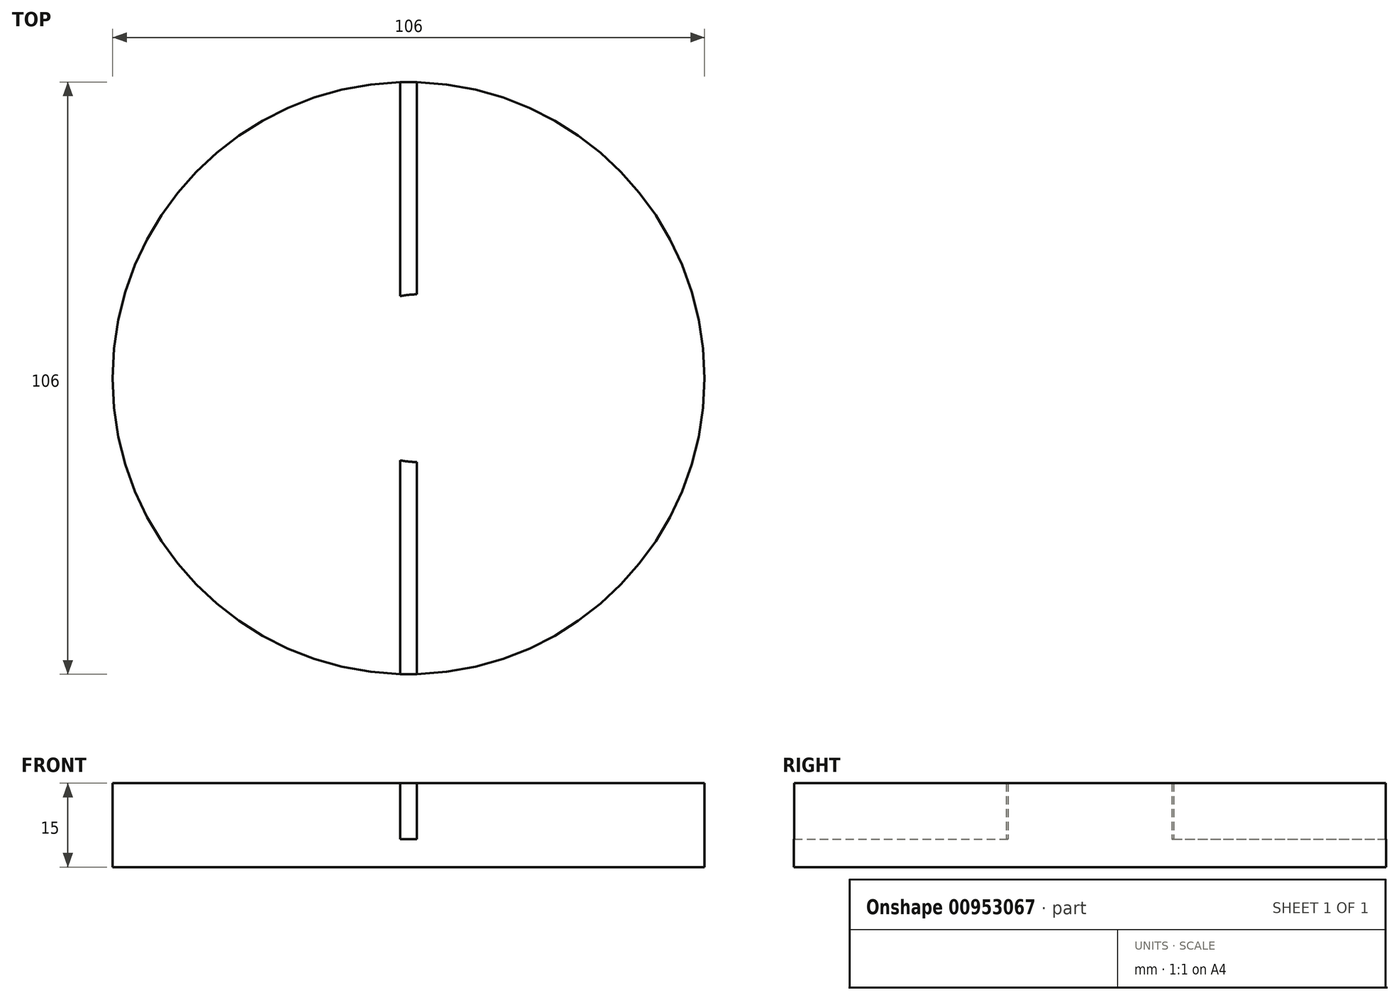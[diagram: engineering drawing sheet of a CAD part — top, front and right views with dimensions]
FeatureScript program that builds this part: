
annotation { "Feature Type Name" : "Feature", "Feature Type Description" : "" }
export const myFeature = defineFeature(function(context is Context, id is Id, definition is map)
    precondition{}
    {
        {
            var Q0;
            Q0=qCreatedBy(makeId("Top.planeOp"),FACE);
            var sketch = newSketch(context, id + "F0", { "sketchPlane" : qUnion([Q0])});
            skCircle(sketch, "E0", {"center": v(0, 0) * mm, "radius": 53 * mm});
            skSolve(sketch);
        }
        {
            var Q0;
            Q0=makeQuery(id+"F0.imprint","IMPRINT",FACE,{"disambiguationData":[TD([[makeQuery(id+"F0.imprint","IMPRINT",EDGE,{"derivedFrom":sQuery(id+"F0.wireOp",EDGE,"E0")}),1.0]])]});
            extrude(context, id + "F1", {"entities" : qUnion([Q0]), "depth" : 15 * mm, "offsetDistance" : 25 * mm});
        }
        {
            var Q0;
            Q0=makeQuery(id+"F1.opExtrude","CAP_FACE",FACE,{"disambiguationData":[OSD([sQuery(id+"F0.wireOp",EDGE,"E0")])],"isStart":false});
            var sketch = newSketch(context, id + "F2", { "sketchPlane" : qUnion([Q0])});
            skLineSegment(sketch, "E1.bottom", {"start": v(1.5, -75) * mm, "end": v(-1.5, -75) * mm});
            skLineSegment(sketch, "E1.top", {"start": v(1.5, 75) * mm, "end": v(-1.5, 75) * mm});
            skLineSegment(sketch, "E1.left", {"start": v(1.5, -75) * mm, "end": v(1.5, 75) * mm});
            skLineSegment(sketch, "E1.right", {"start": v(-1.5, -75) * mm, "end": v(-1.5, 75) * mm});
            skPoint(sketch, "E1.middle", {"position": v(0, 0) * mm});
            skSolve(sketch);
        }
        {
            var Q0;
            {var subQ0=sQuery(id+"F2.wireOp",EDGE,"E1.left");var subQ1=makeQuery(id+"F1.opExtrude","CAP_EDGE",EDGE,{"disambiguationData":[OSD([sQuery(id+"F0.wireOp",EDGE,"E0")])],"isStart":false});var subQ2=makeQuery(id+"F2.imprint","INTERSECT",VERTEX,{"disambiguationData":[OD(0.0)],"derivedFrom":[subQ1,subQ0]});Q0=makeQuery(id+"F2.imprint","IMPRINT",FACE,{"disambiguationData":[TD([[makeQuery(id+"F2.imprint","IMPRINT",EDGE,{"disambiguationData":[TD([[subQ2,-1.0]])],"derivedFrom":subQ0}),1.0]])]});}
            extrude(context, id + "F3", {"entities" : qUnion([Q0]), "operationType" : NewBodyOperationType.REMOVE, "oppositeDirection" : true, "depth" : 10 * mm, "offsetDistance" : 25 * mm});
        }
        {
            var Q0;
            Q0=qCreatedBy(makeId("Right.planeOp"),FACE);
            var sketch = newSketch(context, id + "F4", { "sketchPlane" : qUnion([Q0])});
            skLineSegment(sketch, "E2", {"start": v(0, 0) * mm, "end": v(0, 68.18) * mm, "construction": true});
            skSolve(sketch);
        }
        {
            var Q0;
            {var subQ0=sQuery(id+"F2.wireOp",EDGE,"E1.right");var subQ1=sQuery(id+"F2.wireOp",EDGE,"E1.left");var subQ2=sQuery(id+"F0.wireOp",EDGE,"E0");Q0=makeQuery(id+"FD0Jw6gWIEDZ3Gv_1.5.F3.boolean.opBoolean","MERGE",FACE,{"derivedFrom":[makeQuery(id+"FD0Jw6gWIEDZ3Gv_1.4.F3.boolean.opBoolean","MERGE",FACE,{"derivedFrom":[makeQuery(id+"FD0Jw6gWIEDZ3Gv_1.3.F3.boolean.opBoolean","MERGE",FACE,{"derivedFrom":[makeQuery(id+"FD0Jw6gWIEDZ3Gv_1.2.F3.boolean.opBoolean","MERGE",FACE,{"derivedFrom":[makeQuery(id+"FD0Jw6gWIEDZ3Gv_1.1.F3.boolean.opBoolean","MERGE",FACE,{"derivedFrom":[makeQuery(id+"F3.boolean.opBoolean","COPY",FACE,{"derivedFrom":makeQuery(id+"F3.opExtrude","CAP_FACE",FACE,{"disambiguationData":[OSD([subQ2,subQ1,subQ0])],"isStart":false})})],"fromTools":[makeQuery(id+"FD0Jw6gWIEDZ3Gv_1.1.F3.opExtrude","CAP_FACE",FACE,{"disambiguationData":[OSD([subQ2,subQ1,subQ0])],"isStart":false})]})],"fromTools":[makeQuery(id+"FD0Jw6gWIEDZ3Gv_1.2.F3.opExtrude","CAP_FACE",FACE,{"disambiguationData":[OSD([subQ2,subQ1,subQ0])],"isStart":false})]})],"fromTools":[makeQuery(id+"FD0Jw6gWIEDZ3Gv_1.3.F3.opExtrude","CAP_FACE",FACE,{"disambiguationData":[OSD([subQ2,subQ1,subQ0])],"isStart":false})]})],"fromTools":[makeQuery(id+"FD0Jw6gWIEDZ3Gv_1.4.F3.opExtrude","CAP_FACE",FACE,{"disambiguationData":[OSD([subQ2,subQ1,subQ0])],"isStart":false})]})],"fromTools":[makeQuery(id+"FD0Jw6gWIEDZ3Gv_1.5.F3.opExtrude","CAP_FACE",FACE,{"disambiguationData":[OSD([subQ2,subQ1,subQ0])],"isStart":false})]});}
            var sketch = newSketch(context, id + "F5", { "sketchPlane" : qUnion([Q0])});
            skCircle(sketch, "E3", {"center": v(1.5, 0) * mm, "radius": 15 * mm});
            skSolve(sketch);
        }
        {
            var Q0;
            Q0 = qSketchRegion(id + "F5", true);
            extrude(context, id + "F6", {"entities" : qUnion([Q0]), "operationType" : NewBodyOperationType.ADD, "depth" : 10 * mm, "offsetDistance" : 25 * mm});
        }
    });
